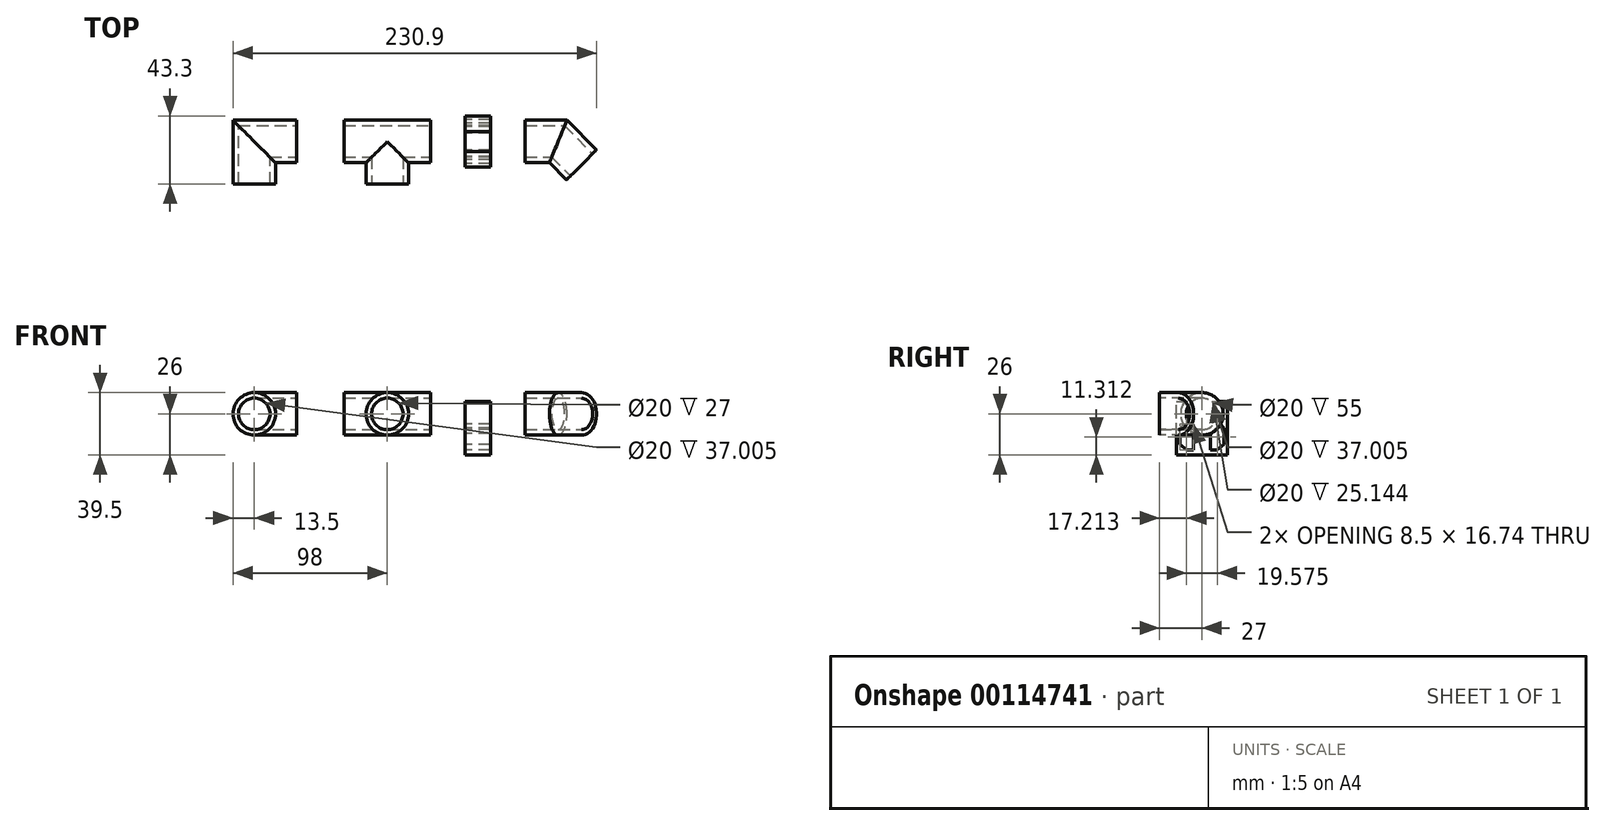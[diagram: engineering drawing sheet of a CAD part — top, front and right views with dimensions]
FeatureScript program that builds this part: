
annotation { "Feature Type Name" : "Feature", "Feature Type Description" : "" }
export const myFeature = defineFeature(function(context is Context, id is Id, definition is map)
    precondition{}
    {
        {
            var Q0;
            Q0=qCreatedBy(makeId("Top.planeOp"),FACE);
            var sketch = newSketch(context, id + "F0", { "sketchPlane" : qUnion([Q0])});
            skLineSegment(sketch, "E0", {"start": v(0, 0) * mm, "end": v(-27, 0) * mm});
            skLineSegment(sketch, "E1", {"start": v(-27, 0) * mm, "end": v(-27, -27) * mm});
            skLineSegment(sketch, "E2.0", {"start": v(-37, 10) * mm, "end": v(-37, -27) * mm});
            skLineSegment(sketch, "E2.1", {"start": v(0, 10) * mm, "end": v(-37, 10) * mm});
            skLineSegment(sketch, "E3.0", {"start": v(-17, -10) * mm, "end": v(-17, -27) * mm});
            skLineSegment(sketch, "E3.1", {"start": v(0, -10) * mm, "end": v(-17, -10) * mm});
            skLineSegment(sketch, "E4", {"start": v(0, 10) * mm, "end": v(0, 0) * mm});
            skLineSegment(sketch, "E5", {"start": v(0, -10) * mm, "end": v(0, 0) * mm});
            skLineSegment(sketch, "E6", {"start": v(-17, -27) * mm, "end": v(-27, -27) * mm});
            skLineSegment(sketch, "E7", {"start": v(-27, -27) * mm, "end": v(-37, -27) * mm});
            skLineSegment(sketch, "E8.0", {"start": v(-40.5, 13.5) * mm, "end": v(-40.5, -27) * mm});
            skLineSegment(sketch, "E8.1", {"start": v(0, 13.5) * mm, "end": v(-40.5, 13.5) * mm});
            skLineSegment(sketch, "E9.0", {"start": v(-13.5, -13.5) * mm, "end": v(-13.5, -27) * mm});
            skLineSegment(sketch, "E9.1", {"start": v(0, -13.5) * mm, "end": v(-13.5, -13.5) * mm});
            skLineSegment(sketch, "E10", {"start": v(0, 13.5) * mm, "end": v(0, 10) * mm});
            skLineSegment(sketch, "E11", {"start": v(0, -10) * mm, "end": v(0, -13.5) * mm});
            skLineSegment(sketch, "E12", {"start": v(-13.5, -27) * mm, "end": v(-17, -27) * mm});
            skLineSegment(sketch, "E13", {"start": v(-37, -27) * mm, "end": v(-40.5, -27) * mm});
            skLineSegment(sketch, "E14", {"start": v(-45.95, 18.95) * mm, "end": v(-7.93, -19.07) * mm});
            skLineSegment(sketch, "E15", {"start": v(0, 0) * mm, "end": v(30, 0) * mm, "construction": true});
            skLineSegment(sketch, "E16", {"start": v(30, 0) * mm, "end": v(57.5, 0) * mm});
            skLineSegment(sketch, "E17", {"start": v(57.5, 0) * mm, "end": v(57.5, -27) * mm});
            skLineSegment(sketch, "E18", {"start": v(57.5, 0) * mm, "end": v(85, 0) * mm});
            skLineSegment(sketch, "E19.0", {"start": v(47.5, -10) * mm, "end": v(47.5, -27) * mm});
            skLineSegment(sketch, "E19.1", {"start": v(30, -10) * mm, "end": v(47.5, -10) * mm});
            skLineSegment(sketch, "E20.0", {"start": v(67.5, -10) * mm, "end": v(85, -10) * mm});
            skLineSegment(sketch, "E20.1", {"start": v(67.5, -10) * mm, "end": v(67.5, -27) * mm});
            skLineSegment(sketch, "E21.0", {"start": v(57.5, 10) * mm, "end": v(85, 10) * mm});
            skLineSegment(sketch, "E21.1", {"start": v(30, 10) * mm, "end": v(57.5, 10) * mm});
            skLineSegment(sketch, "E22.0", {"start": v(57.5, 13.5) * mm, "end": v(85, 13.5) * mm});
            skLineSegment(sketch, "E22.1", {"start": v(30, 13.5) * mm, "end": v(57.5, 13.5) * mm});
            skLineSegment(sketch, "E23.0", {"start": v(44, -13.5) * mm, "end": v(44, -27) * mm});
            skLineSegment(sketch, "E23.1", {"start": v(30, -13.5) * mm, "end": v(44, -13.5) * mm});
            skLineSegment(sketch, "E24.0", {"start": v(71, -13.5) * mm, "end": v(85, -13.5) * mm});
            skLineSegment(sketch, "E24.1", {"start": v(71, -13.5) * mm, "end": v(71, -27) * mm});
            skLineSegment(sketch, "E25", {"start": v(30, 13.5) * mm, "end": v(30, 10) * mm});
            skLineSegment(sketch, "E26", {"start": v(30, 10) * mm, "end": v(30, -10) * mm});
            skLineSegment(sketch, "E27", {"start": v(30, -10) * mm, "end": v(30, -13.5) * mm});
            skLineSegment(sketch, "E28", {"start": v(44, -27) * mm, "end": v(47.5, -27) * mm});
            skLineSegment(sketch, "E29", {"start": v(47.5, -27) * mm, "end": v(67.5, -27) * mm});
            skLineSegment(sketch, "E30", {"start": v(67.5, -27) * mm, "end": v(71, -27) * mm});
            skLineSegment(sketch, "E31", {"start": v(85, -13.5) * mm, "end": v(85, -10) * mm});
            skLineSegment(sketch, "E32", {"start": v(85, -10) * mm, "end": v(85, 0) * mm});
            skLineSegment(sketch, "E33", {"start": v(85, 0) * mm, "end": v(85, 10) * mm});
            skLineSegment(sketch, "E34", {"start": v(85, 10) * mm, "end": v(85, 13.5) * mm});
            skLineSegment(sketch, "E35", {"start": v(85, 0) * mm, "end": v(115, 0) * mm, "construction": true});
            skLineSegment(sketch, "E36", {"start": v(115, 0) * mm, "end": v(145, 0) * mm, "construction": true});
            skLineSegment(sketch, "E37", {"start": v(145, 0) * mm, "end": v(166, 0) * mm});
            skLineSegment(sketch, "E38", {"start": v(166, 0) * mm, "end": v(180.85, -14.85) * mm});
            skLineSegment(sketch, "E39.0", {"start": v(161.86, -10) * mm, "end": v(173.78, -21.92) * mm});
            skLineSegment(sketch, "E39.1", {"start": v(145, -10) * mm, "end": v(161.86, -10) * mm});
            skLineSegment(sketch, "E40.0", {"start": v(160.4, -13.5) * mm, "end": v(171.3, -24.4) * mm});
            skLineSegment(sketch, "E40.1", {"start": v(145, -13.5) * mm, "end": v(160.4, -13.5) * mm});
            skLineSegment(sketch, "E41.0", {"start": v(170.14, 10) * mm, "end": v(187.92, -7.78) * mm});
            skLineSegment(sketch, "E41.1", {"start": v(145, 10) * mm, "end": v(170.14, 10) * mm});
            skLineSegment(sketch, "E42.0", {"start": v(171.6, 13.5) * mm, "end": v(190.4, -5.3) * mm});
            skLineSegment(sketch, "E42.1", {"start": v(145, 13.5) * mm, "end": v(171.6, 13.5) * mm});
            skLineSegment(sketch, "E43", {"start": v(145, 13.5) * mm, "end": v(145, 10) * mm});
            skLineSegment(sketch, "E44", {"start": v(145, 10) * mm, "end": v(145, 0) * mm});
            skLineSegment(sketch, "E45", {"start": v(145, 0) * mm, "end": v(145, -10) * mm});
            skLineSegment(sketch, "E46", {"start": v(145, -10) * mm, "end": v(145, -13.5) * mm});
            skLineSegment(sketch, "E47", {"start": v(180.85, -14.85) * mm, "end": v(173.78, -21.92) * mm});
            skLineSegment(sketch, "E48", {"start": v(173.78, -21.92) * mm, "end": v(171.3, -24.4) * mm});
            skLineSegment(sketch, "E49", {"start": v(180.85, -14.85) * mm, "end": v(187.92, -7.78) * mm});
            skLineSegment(sketch, "E50", {"start": v(187.92, -7.78) * mm, "end": v(190.4, -5.3) * mm});
            skSolve(sketch);
        }
        {
            var Q0;
            Q0=sQuery(id+"F0.wireOp",EDGE,"E13");
            var Q1;
            Q1=sQuery(id+"F0.wireOp",EDGE,"E1");
            revolve(context, id + "F1", {"bodyType" : ToolBodyType.SURFACE, "surfaceEntities" : qUnion([Q0]), "axis" : qUnion([Q1]), "revolveType" : RevolveType.FULL});
        }
        {
            var Q0;
            Q0=makeQuery(id+"F1.opRevolve","SWEPT_FACE",FACE,{"disambiguationData":[OSD([sQuery(id+"F0.wireOp",EDGE,"E13")])]});
            var Q1;
            Q1=sQuery(id+"F0.wireOp",EDGE,"E1");
            var Q2;
            Q2=sQuery(id+"F0.wireOp",EDGE,"E0");
            sweep(context, id + "F2", {"profiles" : qUnion([Q0]), "path" : qUnion([Q1, Q2])});
        }
        {
            var Q0;
            Q0=makeQuery(id+"F1.opRevolve","SWEPT_BODY",BODY,{"disambiguationData":[OSD([sQuery(id+"F0.wireOp",EDGE,"E13")])]});
            deleteBodies(context, id + "F3", {"entities" : qUnion([Q0])});
        }
        {
            var Q0;
            Q0=sQuery(id+"F0.wireOp",EDGE,"E25");
            var Q1;
            Q1=sQuery(id+"F0.wireOp",EDGE,"E16");
            revolve(context, id + "F4", {"bodyType" : ToolBodyType.SURFACE, "surfaceEntities" : qUnion([Q0]), "axis" : qUnion([Q1]), "revolveType" : RevolveType.FULL});
        }
        {
            var Q0;
            Q0=makeQuery(id+"F4.opRevolve","SWEPT_FACE",FACE,{"disambiguationData":[OSD([sQuery(id+"F0.wireOp",EDGE,"E25")])]});
            var Q1;
            Q1=sQuery(id+"F0.wireOp",EDGE,"E16");
            var Q2;
            Q2=sQuery(id+"F0.wireOp",EDGE,"E18");
            sweep(context, id + "F5", {"profiles" : qUnion([Q0]), "path" : qUnion([Q1, Q2])});
        }
        {
            var Q0;
            Q0=makeQuery(id+"F4.opRevolve","SWEPT_BODY",BODY,{"disambiguationData":[OSD([sQuery(id+"F0.wireOp",EDGE,"E25")])]});
            deleteBodies(context, id + "F6", {"entities" : qUnion([Q0])});
        }
        {
            var Q0;
            Q0=sQuery(id+"F0.wireOp",EDGE,"E17");
            var Q1;
            Q1=sQuery(id+"F0.wireOp",VERTEX,"E17.end");
            cPlane(context, id + "F7", {"entities" : qUnion([Q0, Q1]), "cplaneType" : CPlaneType.LINE_POINT, "offset" : 25 * mm, "width" : 150 * mm, "height" : 150 * mm});
        }
        {
            var Q0;
            Q0=qCreatedBy(id+"F7.planeOp",FACE);
            var sketch = newSketch(context, id + "F8", { "sketchPlane" : qUnion([Q0])});
            skPoint(sketch, "E51.0", {"position": v(57.5, 0) * mm});
            skPoint(sketch, "E52.0", {"position": v(47.5, 0) * mm});
            skPoint(sketch, "E53.0", {"position": v(44, 0) * mm});
            skCircle(sketch, "E54", {"center": v(57.5, 0) * mm, "radius": 10 * mm});
            skCircle(sketch, "E55", {"center": v(57.5, 0) * mm, "radius": 13.5 * mm});
            skSolve(sketch);
        }
        {
            var Q0;
            Q0=makeQuery(id+"F8.imprint","IMPRINT",FACE,{"disambiguationData":[TD([[makeQuery(id+"F8.imprint","IMPRINT",EDGE,{"derivedFrom":sQuery(id+"F8.wireOp",EDGE,"E54")}),-1.0]])]});
            extrude(context, id + "F9", {"entities" : qUnion([Q0]), "operationType" : NewBodyOperationType.ADD, "endBound" : BoundingType.UP_TO_NEXT, "oppositeDirection" : true, "depth" : 25 * mm});
        }
        {
            var Q0;
            Q0=makeQuery(id+"F8.imprint","IMPRINT",FACE,{"disambiguationData":[TD([[makeQuery(id+"F8.imprint","IMPRINT",EDGE,{"derivedFrom":sQuery(id+"F8.wireOp",EDGE,"E54")}),1.0]])]});
            var Q1;
            Q1=makeQuery(id+"F5.opSweep","SWEPT_FACE",FACE,{"disambiguationData":[OSD([sQuery(id+"F0.wireOp",VERTEX,"E25.end"),sQuery(id+"F0.wireOp",EDGE,"E18")])]});
            extrude(context, id + "F10", {"entities" : qUnion([Q0]), "operationType" : NewBodyOperationType.REMOVE, "endBound" : BoundingType.UP_TO_SURFACE, "oppositeDirection" : true, "endBoundEntityFace" : qUnion([Q1]), "depth" : 25 * mm});
        }
        {
            var Q0;
            Q0=sQuery(id+"F0.wireOp",EDGE,"E35");
            var Q1;
            Q1=sQuery(id+"F0.wireOp",VERTEX,"E35.end");
            cPlane(context, id + "F11", {"entities" : qUnion([Q0, Q1]), "cplaneType" : CPlaneType.LINE_POINT, "offset" : 25 * mm, "width" : 150 * mm, "height" : 150 * mm});
        }
        {
            var Q0;
            Q0=qCreatedBy(id+"F11.planeOp",FACE);
            var sketch = newSketch(context, id + "F12", { "sketchPlane" : qUnion([Q0])});
            skPoint(sketch, "E56.0", {"position": v(0, 0) * mm});
            skPoint(sketch, "E57.0", {"position": v(-10, 0) * mm});
            skCircle(sketch, "E58", {"center": v(0, 0) * mm, "radius": 10 * mm});
            skLineSegment(sketch, "E59", {"start": v(0, -10) * mm, "end": v(0, -10) * mm});
            skLineSegment(sketch, "E60.bottom", {"start": v(-16.3, -10) * mm, "end": v(0, -10) * mm});
            skLineSegment(sketch, "E60.top", {"start": v(-16.3, -26) * mm, "end": v(16.3, -26) * mm});
            skLineSegment(sketch, "E60.left", {"start": v(-16.3, -10) * mm, "end": v(-16.3, -26) * mm});
            skLineSegment(sketch, "E60.right", {"start": v(16.3, -10) * mm, "end": v(16.3, -26) * mm});
            skLineSegment(sketch, "E61", {"start": v(0, -10) * mm, "end": v(0, -26) * mm});
            skLineSegment(sketch, "E62", {"start": v(0, -10) * mm, "end": v(16.3, -10) * mm});
            skLineSegment(sketch, "E63.bottom", {"start": v(-16.3, -10) * mm, "end": v(16.3, -10) * mm});
            skLineSegment(sketch, "E63.top", {"start": v(-16.3, 7.8) * mm, "end": v(16.3, 7.8) * mm});
            skLineSegment(sketch, "E63.left", {"start": v(-16.3, -10) * mm, "end": v(-16.3, 7.8) * mm});
            skLineSegment(sketch, "E63.right", {"start": v(16.3, -10) * mm, "end": v(16.3, 7.8) * mm});
            skLineSegment(sketch, "E64", {"start": v(-11.59, -6.32) * mm, "end": v(-5.54, -12.36) * mm});
            skLineSegment(sketch, "E65", {"start": v(-5.54, -12.36) * mm, "end": v(-5.54, -23.06) * mm});
            skLineSegment(sketch, "E66", {"start": v(-5.54, -23.06) * mm, "end": v(-9.65, -23.06) * mm});
            skLineSegment(sketch, "E67", {"start": v(-9.65, -23.06) * mm, "end": v(-14.04, -19.48) * mm});
            skLineSegment(sketch, "E68", {"start": v(-14.04, -19.48) * mm, "end": v(-14.04, -8.97) * mm});
            skLineSegment(sketch, "E69", {"start": v(-14.04, -8.97) * mm, "end": v(-11.59, -6.32) * mm});
            skLineSegment(sketch, "E70.MirrorCS", {"start": v(11.59, -6.32) * mm, "end": v(5.54, -12.36) * mm});
            skLineSegment(sketch, "E71.MirrorCS", {"start": v(14.04, -8.97) * mm, "end": v(11.59, -6.32) * mm});
            skLineSegment(sketch, "E72.MirrorCS", {"start": v(14.04, -19.48) * mm, "end": v(14.04, -8.97) * mm});
            skLineSegment(sketch, "E73.MirrorCS", {"start": v(9.65, -23.06) * mm, "end": v(14.04, -19.48) * mm});
            skLineSegment(sketch, "E74.MirrorCS", {"start": v(5.54, -23.06) * mm, "end": v(9.65, -23.06) * mm});
            skLineSegment(sketch, "E75.MirrorCS", {"start": v(5.54, -12.36) * mm, "end": v(5.54, -23.06) * mm});
            skSolve(sketch);
        }
        {
            var Q0;
            {var subQ5=sQuery(id+"F12.wireOp",EDGE,"E63.left");Q0=makeQuery(id+"F12.imprint","IMPRINT",FACE,{"disambiguationData":[TD([[makeQuery(id+"F12.imprint","IMPRINT",EDGE,{"derivedFrom":subQ5}),-1.0]])]});}
            var Q1;
            {var subQ5=sQuery(id+"F12.wireOp",EDGE,"E63.right");Q1=makeQuery(id+"F12.imprint","IMPRINT",FACE,{"disambiguationData":[TD([[makeQuery(id+"F12.imprint","IMPRINT",EDGE,{"derivedFrom":subQ5}),1.0]])]});}
            var Q2;
            {var subQ0=sQuery(id+"F12.wireOp",EDGE,"E60.right");Q2=makeQuery(id+"F12.imprint","IMPRINT",FACE,{"disambiguationData":[TD([[makeQuery(id+"F12.imprint","IMPRINT",EDGE,{"derivedFrom":subQ0}),-1.0]])]});}
            var Q3;
            {var subQ0=sQuery(id+"F12.wireOp",EDGE,"E60.left");Q3=makeQuery(id+"F12.imprint","IMPRINT",FACE,{"disambiguationData":[TD([[makeQuery(id+"F12.imprint","IMPRINT",EDGE,{"derivedFrom":subQ0}),1.0]])]});}
            extrude(context, id + "F13", {"entities" : qUnion([Q0, Q1, Q2, Q3]), "endBound" : BoundingType.SYMMETRIC, "depth" : 16 * mm});
        }
        {
            var Q0;
            Q0=sQuery(id+"F0.wireOp",EDGE,"E43");
            var Q1;
            Q1=sQuery(id+"F0.wireOp",EDGE,"E37");
            revolve(context, id + "F14", {"bodyType" : ToolBodyType.SURFACE, "surfaceEntities" : qUnion([Q0]), "axis" : qUnion([Q1]), "revolveType" : RevolveType.FULL});
        }
        {
            var Q0;
            Q0=makeQuery(id+"F14.opRevolve","SWEPT_FACE",FACE,{"disambiguationData":[OSD([sQuery(id+"F0.wireOp",EDGE,"E43")])]});
            var Q1;
            Q1=sQuery(id+"F0.wireOp",EDGE,"E37");
            var Q2;
            Q2=sQuery(id+"F0.wireOp",EDGE,"E38");
            sweep(context, id + "F15", {"profiles" : qUnion([Q0]), "path" : qUnion([Q1, Q2])});
        }
        {
            var Q0;
            Q0=makeQuery(id+"F14.opRevolve","SWEPT_FACE",FACE,{"disambiguationData":[OSD([sQuery(id+"F0.wireOp",EDGE,"E43")])]});
            var sketch = newSketch(context, id + "F16", { "sketchPlane" : qUnion([Q0])});
            skPoint(sketch, "E76.0", {"position": v(0, 0) * mm});
            skCircle(sketch, "E77.0", {"center": v(0, 0) * mm, "radius": 13.5 * mm});
            skPoint(sketch, "E78", {"position": v(0, 13.5) * mm});
            skSolve(sketch);
        }
        {
            var Q0;
            Q0=qCreatedBy(makeId("Top.planeOp"),FACE);
            var Q1;
            Q1=sQuery(id+"F16.wireOp",VERTEX,"E78");
            cPlane(context, id + "F17", {"entities" : qUnion([Q0, Q1]), "cplaneType" : CPlaneType.PLANE_POINT, "offset" : 25 * mm, "width" : 150 * mm, "height" : 150 * mm});
        }
        {
            var Q0;
            Q0=makeQuery(id+"F14.opRevolve","SWEPT_BODY",BODY,{"disambiguationData":[OSD([sQuery(id+"F0.wireOp",EDGE,"E43")])]});
            deleteBodies(context, id + "F18", {"entities" : qUnion([Q0])});
        }
    });
